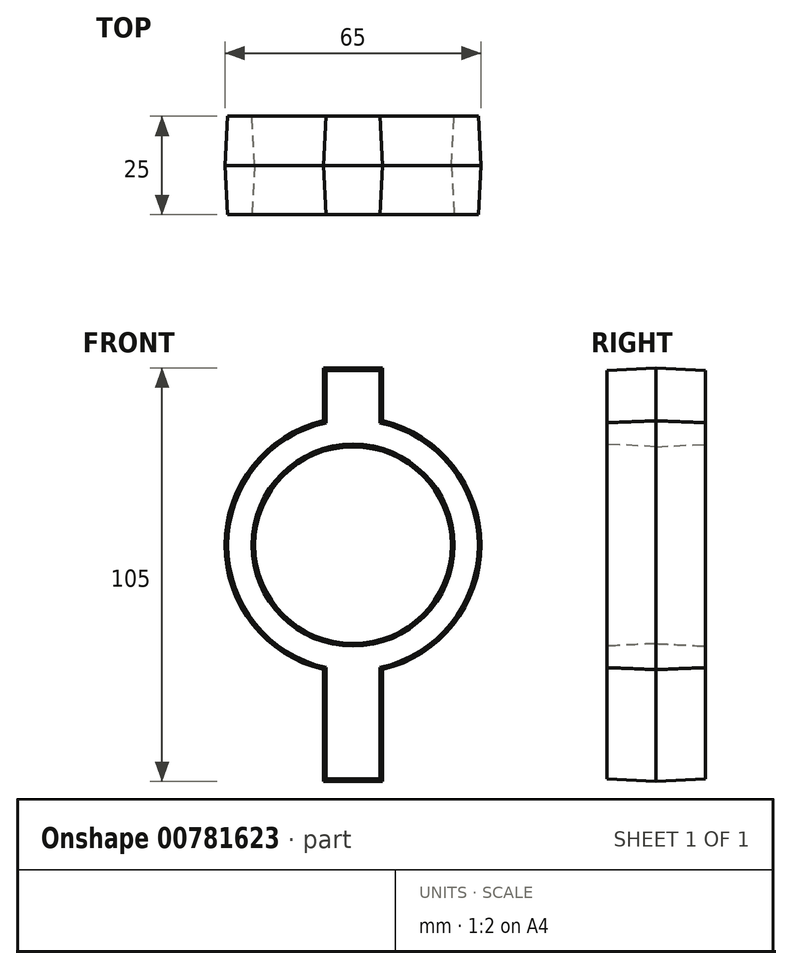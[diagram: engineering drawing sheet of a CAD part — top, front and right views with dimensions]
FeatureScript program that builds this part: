
annotation { "Feature Type Name" : "Feature", "Feature Type Description" : "" }
export const myFeature = defineFeature(function(context is Context, id is Id, definition is map)
    precondition{}
    {
        {
            var Q0;
            Q0=qCreatedBy(makeId("Front.planeOp"),FACE);
            var sketch = newSketch(context, id + "F0", { "sketchPlane" : qUnion([Q0])});
            skCircle(sketch, "E0", {"center": v(0, 0) * mm, "radius": 25 * mm});
            skArc(sketch, "E1", {"start": v(-7.5, 31.62) * mm, "mid": v(-32.5, 0) * mm, "end": v(-7.5, -31.62) * mm});
            skLineSegment(sketch, "E2.bottom", {"start": v(7.5, 45) * mm, "end": v(-7.5, 45) * mm});
            skLineSegment(sketch, "E2.top", {"start": v(7.5, -60) * mm, "end": v(-7.5, -60) * mm});
            skLineSegment(sketch, "E2.left", {"start": v(7.5, 45) * mm, "end": v(7.5, 31.62) * mm});
            skLineSegment(sketch, "E2.right", {"start": v(-7.5, 45) * mm, "end": v(-7.5, 31.62) * mm});
            skLineSegment(sketch, "E3.trimOffspring", {"start": v(7.5, -31.62) * mm, "end": v(7.5, -60) * mm});
            skLineSegment(sketch, "E4.trimOffspring", {"start": v(-7.5, -31.62) * mm, "end": v(-7.5, -60) * mm});
            skArc(sketch, "E5.trimOffspring", {"start": v(7.5, -31.62) * mm, "mid": v(32.5, 0) * mm, "end": v(7.5, 31.62) * mm});
            skSolve(sketch);
        }
        {
            var Q0;
            Q0=makeQuery(id+"F0.imprint","IMPRINT",FACE,{"disambiguationData":[TD([[makeQuery(id+"F0.imprint","IMPRINT",EDGE,{"derivedFrom":sQuery(id+"F0.wireOp",EDGE,"E0")}),-1.0]])]});
            extrude(context, id + "F1", {"entities" : qUnion([Q0]), "endBound" : BoundingType.SYMMETRIC, "depth" : 25 * mm, "offsetDistance" : 25 * mm, "hasDraft" : true, "draftAngle" : 3 * degree, "draftPullDirection" : true});
        }
    });
